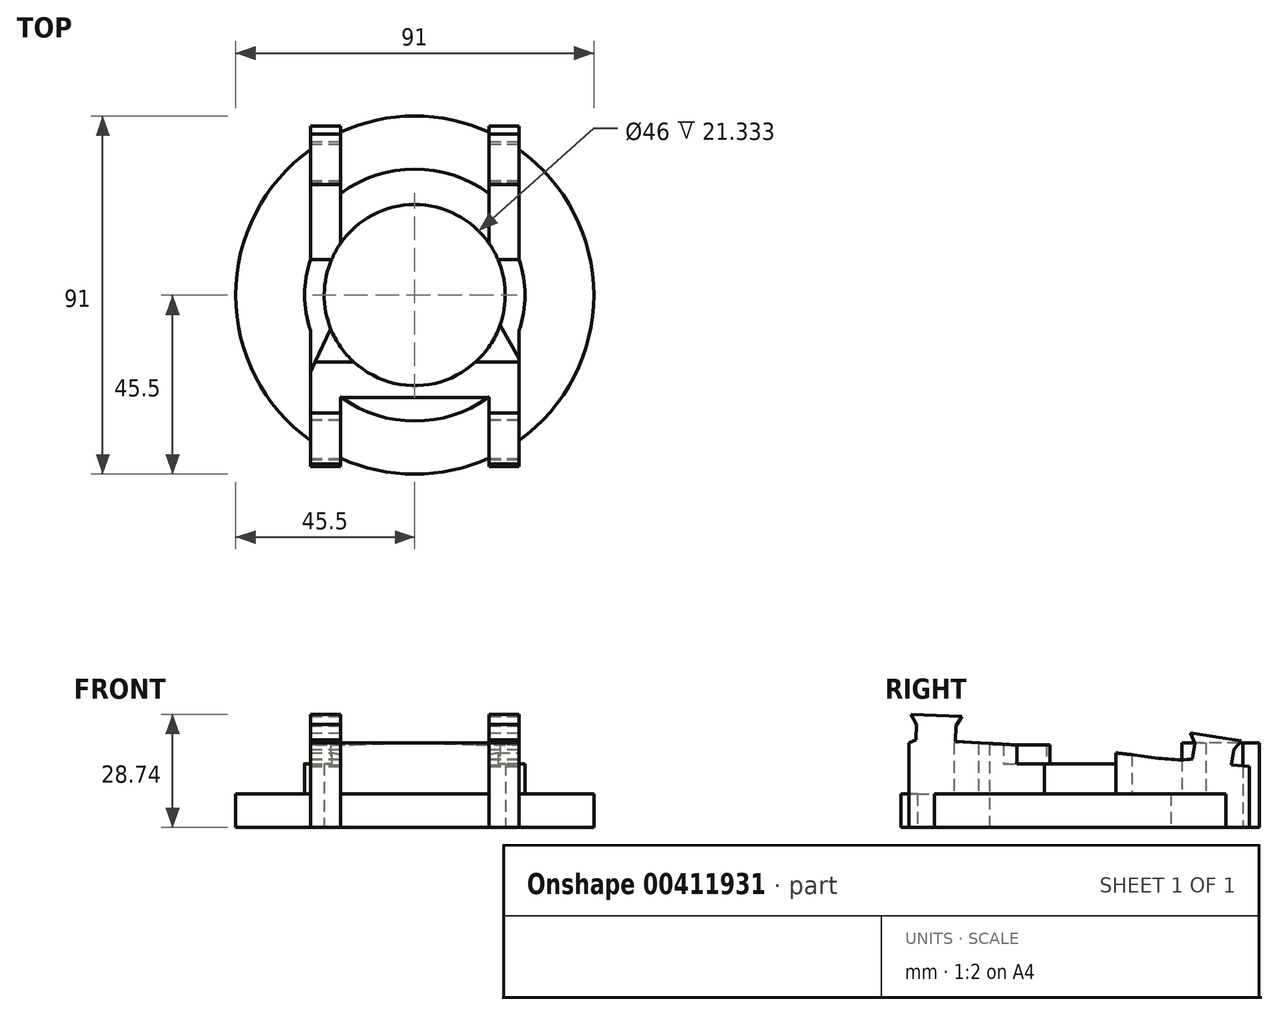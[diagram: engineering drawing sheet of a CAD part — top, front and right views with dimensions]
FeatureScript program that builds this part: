
annotation { "Feature Type Name" : "Feature", "Feature Type Description" : "" }
export const myFeature = defineFeature(function(context is Context, id is Id, definition is map)
    precondition{}
    {
        {
            var Q0;
            Q0=qCreatedBy(makeId("Top.planeOp"),FACE);
            var sketch = newSketch(context, id + "F0", { "sketchPlane" : qUnion([Q0])});
            skLineSegment(sketch, "E0", {"start": v(0, 45.5) * mm, "end": v(0, -45.5) * mm, "construction": true});
            skLineSegment(sketch, "E1", {"start": v(-45.7, 0) * mm, "end": v(45.55, 0) * mm, "construction": true});
            skCircle(sketch, "E2", {"center": v(0, 0) * mm, "radius": 23 * mm});
            skCircle(sketch, "E3", {"center": v(0, 0) * mm, "radius": 45.5 * mm});
            skArc(sketch, "E4", {"start": v(-26.5, 9.04) * mm, "mid": v(-28, 0) * mm, "end": v(-26.5, -9.04) * mm});
            skArc(sketch, "E5", {"start": v(-18.9, 25.82) * mm, "mid": v(0, 32) * mm, "end": v(18.9, 25.82) * mm});
            skArc(sketch, "E6", {"start": v(-18.9, -25.82) * mm, "mid": v(0, -32) * mm, "end": v(18.9, -25.82) * mm});
            skLineSegment(sketch, "E7.bottom", {"start": v(-26.5, 42.99) * mm, "end": v(-18.9, 42.99) * mm});
            skLineSegment(sketch, "E7.top", {"start": v(-26.5, -43.51) * mm, "end": v(-18.9, -43.51) * mm});
            skLineSegment(sketch, "E7.left", {"start": v(-26.5, 42.99) * mm, "end": v(-26.5, 9.04) * mm});
            skLineSegment(sketch, "E7.right", {"start": v(26.5, 42.99) * mm, "end": v(26.5, 9.04) * mm});
            skLineSegment(sketch, "E8.left", {"start": v(-18.9, 42.99) * mm, "end": v(-18.9, 13.1) * mm});
            skLineSegment(sketch, "E8.right", {"start": v(18.9, 42.99) * mm, "end": v(18.9, 13.1) * mm});
            skLineSegment(sketch, "E9", {"start": v(-26.5, 9.04) * mm, "end": v(-21.15, 9.04) * mm});
            skLineSegment(sketch, "E10", {"start": v(26.5, 9.04) * mm, "end": v(21.15, 9.04) * mm});
            skLineSegment(sketch, "E11.trimOffspring", {"start": v(-18.9, -13.1) * mm, "end": v(-18.9, -43.51) * mm});
            skLineSegment(sketch, "E12.trimOffspring", {"start": v(18.9, -13.1) * mm, "end": v(18.9, -43.51) * mm});
            skLineSegment(sketch, "E13.trimOffspring", {"start": v(-26.5, -9.04) * mm, "end": v(-26.5, -43.51) * mm});
            skLineSegment(sketch, "E14.trimOffspring", {"start": v(26.5, -9.04) * mm, "end": v(26.5, -43.51) * mm});
            skArc(sketch, "E15.trimOffspring", {"start": v(26.5, -9.04) * mm, "mid": v(28, 0) * mm, "end": v(26.5, 9.04) * mm});
            skLineSegment(sketch, "E16", {"start": v(-26.5, -19.54) * mm, "end": v(-21.34, -8.59) * mm});
            skLineSegment(sketch, "E17", {"start": v(26.5, -16.1) * mm, "end": v(21.69, -7.65) * mm});
            skLineSegment(sketch, "E18.trimOffspring", {"start": v(18.9, 42.99) * mm, "end": v(26.5, 42.99) * mm});
            skLineSegment(sketch, "E19.trimOffspring", {"start": v(18.9, -43.51) * mm, "end": v(26.5, -43.51) * mm});
            skSolve(sketch);
        }
        {
            var Q0;
            Q0=qCreatedBy(makeId("Right.planeOp"),FACE);
            var sketch = newSketch(context, id + "F1", { "sketchPlane" : qUnion([Q0])});
            skLineSegment(sketch, "E20", {"start": v(0, 0) * mm, "end": v(0, 30.19) * mm, "construction": true});
            skLineSegment(sketch, "E21", {"start": v(0, 30.19) * mm, "end": v(-43.27, 30.19) * mm, "construction": true});
            skSolve(sketch);
        }
        {
            var Q0;
            {var subQ1=sQuery(id+"F0.wireOp",EDGE,"E4");Q0=makeQuery(id+"F0.imprint","IMPRINT",FACE,{"disambiguationData":[TD([[makeQuery(id+"F0.imprint","IMPRINT",EDGE,{"derivedFrom":subQ1}),-1.0]])]});}
            var Q1;
            {var subQ5=sQuery(id+"F0.wireOp",EDGE,"E6");Q1=makeQuery(id+"F0.imprint","IMPRINT",FACE,{"disambiguationData":[TD([[makeQuery(id+"F0.imprint","IMPRINT",EDGE,{"derivedFrom":subQ5}),-1.0]])]});}
            var Q2;
            {var subQ4=sQuery(id+"F0.wireOp",EDGE,"E15.trimOffspring");Q2=makeQuery(id+"F0.imprint","IMPRINT",FACE,{"disambiguationData":[TD([[makeQuery(id+"F0.imprint","IMPRINT",EDGE,{"derivedFrom":subQ4}),-1.0]])]});}
            var Q3;
            {var subQ5=sQuery(id+"F0.wireOp",EDGE,"E5");Q3=makeQuery(id+"F0.imprint","IMPRINT",FACE,{"disambiguationData":[TD([[makeQuery(id+"F0.imprint","IMPRINT",EDGE,{"derivedFrom":subQ5}),1.0]])]});}
            var Q4;
            {var subQ6=sQuery(id+"F0.wireOp",EDGE,"E16");Q4=makeQuery(id+"F0.imprint","IMPRINT",FACE,{"disambiguationData":[TD([[makeQuery(id+"F0.imprint","IMPRINT",EDGE,{"derivedFrom":subQ6}),-1.0]])]});}
            var Q5;
            {var subQ5=sQuery(id+"F0.wireOp",EDGE,"E6");Q5=makeQuery(id+"F0.imprint","IMPRINT",FACE,{"disambiguationData":[TD([[makeQuery(id+"F0.imprint","IMPRINT",EDGE,{"derivedFrom":subQ5}),1.0]])]});}
            var Q6;
            {var subQ4=sQuery(id+"F0.wireOp",EDGE,"E17");Q6=makeQuery(id+"F0.imprint","IMPRINT",FACE,{"disambiguationData":[TD([[makeQuery(id+"F0.imprint","IMPRINT",EDGE,{"derivedFrom":subQ4}),1.0]])]});}
            var Q7;
            {var subQ0=sQuery(id+"F0.wireOp",EDGE,"E10");Q7=makeQuery(id+"F0.imprint","IMPRINT",FACE,{"disambiguationData":[TD([[makeQuery(id+"F0.imprint","IMPRINT",EDGE,{"derivedFrom":subQ0}),1.0]])]});}
            var Q8;
            {var subQ4=sQuery(id+"F0.wireOp",EDGE,"E10");Q8=makeQuery(id+"F0.imprint","IMPRINT",FACE,{"disambiguationData":[TD([[makeQuery(id+"F0.imprint","IMPRINT",EDGE,{"derivedFrom":subQ4}),-1.0]])]});}
            var Q9;
            {var subQ5=sQuery(id+"F0.wireOp",EDGE,"E5");Q9=makeQuery(id+"F0.imprint","IMPRINT",FACE,{"disambiguationData":[TD([[makeQuery(id+"F0.imprint","IMPRINT",EDGE,{"derivedFrom":subQ5}),-1.0]])]});}
            var Q10;
            {var subQ2=sQuery(id+"F0.wireOp",EDGE,"E9");Q10=makeQuery(id+"F0.imprint","IMPRINT",FACE,{"disambiguationData":[TD([[makeQuery(id+"F0.imprint","IMPRINT",EDGE,{"derivedFrom":subQ2}),1.0]])]});}
            var Q11;
            {var subQ2=sQuery(id+"F0.wireOp",EDGE,"E4");Q11=makeQuery(id+"F0.imprint","IMPRINT",FACE,{"disambiguationData":[TD([[makeQuery(id+"F0.imprint","IMPRINT",EDGE,{"derivedFrom":subQ2}),1.0]])]});}
            var Q12;
            {var subQ5=sQuery(id+"F0.wireOp",EDGE,"E7.bottom");Q12=makeQuery(id+"F0.imprint","IMPRINT",FACE,{"disambiguationData":[TD([[makeQuery(id+"F0.imprint","IMPRINT",EDGE,{"derivedFrom":subQ5}),-1.0]])]});}
            var Q13;
            {var subQ5=sQuery(id+"F0.wireOp",EDGE,"E18.trimOffspring");Q13=makeQuery(id+"F0.imprint","IMPRINT",FACE,{"disambiguationData":[TD([[makeQuery(id+"F0.imprint","IMPRINT",EDGE,{"derivedFrom":subQ5}),-1.0]])]});}
            var Q14;
            {var subQ5=sQuery(id+"F0.wireOp",EDGE,"E19.trimOffspring");Q14=makeQuery(id+"F0.imprint","IMPRINT",FACE,{"disambiguationData":[TD([[makeQuery(id+"F0.imprint","IMPRINT",EDGE,{"derivedFrom":subQ5}),1.0]])]});}
            var Q15;
            {var subQ5=sQuery(id+"F0.wireOp",EDGE,"E7.top");Q15=makeQuery(id+"F0.imprint","IMPRINT",FACE,{"disambiguationData":[TD([[makeQuery(id+"F0.imprint","IMPRINT",EDGE,{"derivedFrom":subQ5}),1.0]])]});}
            extrude(context, id + "F2", {"entities" : qUnion([Q0, Q1, Q2, Q3, Q4, Q5, Q6, Q7, Q8, Q9, Q10, Q11, Q12, Q13, Q14, Q15]), "depth" : 8.5 * mm});
        }
        {
            var Q0;
            {var subQ6=sQuery(id+"F0.wireOp",EDGE,"E16");Q0=makeQuery(id+"F0.imprint","IMPRINT",FACE,{"disambiguationData":[TD([[makeQuery(id+"F0.imprint","IMPRINT",EDGE,{"derivedFrom":subQ6}),-1.0]])]});}
            var Q1;
            {var subQ2=sQuery(id+"F0.wireOp",EDGE,"E9");Q1=makeQuery(id+"F0.imprint","IMPRINT",FACE,{"disambiguationData":[TD([[makeQuery(id+"F0.imprint","IMPRINT",EDGE,{"derivedFrom":subQ2}),1.0]])]});}
            var Q2;
            {var subQ4=sQuery(id+"F0.wireOp",EDGE,"E10");Q2=makeQuery(id+"F0.imprint","IMPRINT",FACE,{"disambiguationData":[TD([[makeQuery(id+"F0.imprint","IMPRINT",EDGE,{"derivedFrom":subQ4}),-1.0]])]});}
            var Q3;
            {var subQ4=sQuery(id+"F0.wireOp",EDGE,"E17");Q3=makeQuery(id+"F0.imprint","IMPRINT",FACE,{"disambiguationData":[TD([[makeQuery(id+"F0.imprint","IMPRINT",EDGE,{"derivedFrom":subQ4}),1.0]])]});}
            var Q4;
            {var subQ5=sQuery(id+"F0.wireOp",EDGE,"E7.top");Q4=makeQuery(id+"F0.imprint","IMPRINT",FACE,{"disambiguationData":[TD([[makeQuery(id+"F0.imprint","IMPRINT",EDGE,{"derivedFrom":subQ5}),1.0]])]});}
            var Q5;
            {var subQ5=sQuery(id+"F0.wireOp",EDGE,"E19.trimOffspring");Q5=makeQuery(id+"F0.imprint","IMPRINT",FACE,{"disambiguationData":[TD([[makeQuery(id+"F0.imprint","IMPRINT",EDGE,{"derivedFrom":subQ5}),1.0]])]});}
            var Q6;
            {var subQ5=sQuery(id+"F0.wireOp",EDGE,"E18.trimOffspring");Q6=makeQuery(id+"F0.imprint","IMPRINT",FACE,{"disambiguationData":[TD([[makeQuery(id+"F0.imprint","IMPRINT",EDGE,{"derivedFrom":subQ5}),-1.0]])]});}
            var Q7;
            {var subQ5=sQuery(id+"F0.wireOp",EDGE,"E7.bottom");Q7=makeQuery(id+"F0.imprint","IMPRINT",FACE,{"disambiguationData":[TD([[makeQuery(id+"F0.imprint","IMPRINT",EDGE,{"derivedFrom":subQ5}),-1.0]])]});}
            extrude(context, id + "F3", {"entities" : qUnion([Q0, Q1, Q2, Q3, Q4, Q5, Q6, Q7]), "operationType" : NewBodyOperationType.ADD, "depth" : 29 * mm});
        }
        {
            var Q0;
            {var subQ2=sQuery(id+"F0.wireOp",EDGE,"E4");Q0=makeQuery(id+"F0.imprint","IMPRINT",FACE,{"disambiguationData":[TD([[makeQuery(id+"F0.imprint","IMPRINT",EDGE,{"derivedFrom":subQ2}),1.0]])]});}
            var Q1;
            {var subQ0=sQuery(id+"F0.wireOp",EDGE,"E10");Q1=makeQuery(id+"F0.imprint","IMPRINT",FACE,{"disambiguationData":[TD([[makeQuery(id+"F0.imprint","IMPRINT",EDGE,{"derivedFrom":subQ0}),1.0]])]});}
            extrude(context, id + "F4", {"entities" : qUnion([Q0, Q1]), "operationType" : NewBodyOperationType.ADD, "depth" : 16.2 * mm});
        }
        {
            var Q0;
            {var subQ5=sQuery(id+"F0.wireOp",EDGE,"E5");Q0=makeQuery(id+"F0.imprint","IMPRINT",FACE,{"disambiguationData":[TD([[makeQuery(id+"F0.imprint","IMPRINT",EDGE,{"derivedFrom":subQ5}),-1.0]])]});}
            var Q1;
            {var subQ5=sQuery(id+"F0.wireOp",EDGE,"E6");Q1=makeQuery(id+"F0.imprint","IMPRINT",FACE,{"disambiguationData":[TD([[makeQuery(id+"F0.imprint","IMPRINT",EDGE,{"derivedFrom":subQ5}),1.0]])]});}
            extrude(context, id + "F5", {"entities" : qUnion([Q0, Q1]), "operationType" : NewBodyOperationType.ADD, "depth" : 21.5 * mm});
        }
        {
            var Q0;
            {var subQ0=sQuery(id+"F0.wireOp",EDGE,"E14.trimOffspring");Q0=makeQuery(id+"F4.boolean.opBoolean","MERGE",FACE,{"derivedFrom":[makeQuery(id+"F3.boolean.opBoolean","MERGE",FACE,{"derivedFrom":[makeQuery(id+"F2.opExtrude","SWEPT_FACE",FACE,{"disambiguationData":[OSD([subQ0])]}),makeQuery(id+"F3.opExtrude","SWEPT_FACE",FACE,{"disambiguationData":[OSD([subQ0])]})]}),makeQuery(id+"F4.opExtrude","SWEPT_FACE",FACE,{"disambiguationData":[OSD([subQ0])]})]});}
            var sketch = newSketch(context, id + "F6", { "sketchPlane" : qUnion([Q0])});
            skLineSegment(sketch, "E22", {"start": v(-17, 21) * mm, "end": v(-31.7, 21.81) * mm});
            skLineSegment(sketch, "E23", {"start": v(-31.7, 21.81) * mm, "end": v(-31.55, 25.81) * mm});
            skLineSegment(sketch, "E24", {"start": v(-31.55, 25.81) * mm, "end": v(-29.96, 28.26) * mm});
            skLineSegment(sketch, "E25", {"start": v(-29.96, 28.26) * mm, "end": v(-42.95, 28.74) * mm});
            skLineSegment(sketch, "E26", {"start": v(-41.55, 26.18) * mm, "end": v(-42.95, 28.74) * mm});
            skLineSegment(sketch, "E27", {"start": v(-41.55, 26.18) * mm, "end": v(-41.7, 22.19) * mm});
            skLineSegment(sketch, "E28", {"start": v(-41.7, 22.19) * mm, "end": v(-43.51, 21.5) * mm});
            skLineSegment(sketch, "E29", {"start": v(-36.46, 28.5) * mm, "end": v(-36.7, 22) * mm, "construction": true});
            skLineSegment(sketch, "E30", {"start": v(-43.51, 21.5) * mm, "end": v(-43.51, 29) * mm});
            skLineSegment(sketch, "E31", {"start": v(-43.51, 29) * mm, "end": v(-7.6, 29) * mm});
            skLineSegment(sketch, "E32", {"start": v(-7.6, 29) * mm, "end": v(-7.6, 21) * mm});
            skLineSegment(sketch, "E33", {"start": v(-7.6, 21) * mm, "end": v(-17, 21) * mm});
            skLineSegment(sketch, "E34", {"start": v(43, 15.5) * mm, "end": v(38.44, 15.84) * mm});
            skLineSegment(sketch, "E35", {"start": v(38.44, 15.84) * mm, "end": v(39.05, 19.8) * mm});
            skLineSegment(sketch, "E36", {"start": v(39.05, 19.8) * mm, "end": v(40.91, 22.03) * mm});
            skLineSegment(sketch, "E37", {"start": v(40.91, 22.03) * mm, "end": v(28.07, 24.01) * mm});
            skLineSegment(sketch, "E38", {"start": v(28.07, 24.01) * mm, "end": v(29.17, 21.32) * mm});
            skLineSegment(sketch, "E39", {"start": v(29.17, 21.32) * mm, "end": v(28.56, 17.36) * mm});
            skFitSpline(sketch, "E40", {"points": [v(28.56, 17.36) * mm, v(8.2, 19) * mm], "startDerivative": vector(-16.98, -2.06) * mm, "endDerivative": vector(-22.2, 1.8) * mm});
            skLineSegment(sketch, "E41", {"start": v(8.2, 19) * mm, "end": v(8.2, 29) * mm});
            skLineSegment(sketch, "E42", {"start": v(8.2, 29) * mm, "end": v(43, 29) * mm});
            skLineSegment(sketch, "E43", {"start": v(43, 29) * mm, "end": v(43, 15.5) * mm});
            skLineSegment(sketch, "E44", {"start": v(34.5, 23.02) * mm, "end": v(33.5, 16.6) * mm, "construction": true});
            skLineSegment(sketch, "E45", {"start": v(28.56, 17.36) * mm, "end": v(38.44, 15.84) * mm, "construction": true});
            skLineSegment(sketch, "E46", {"start": v(-41.7, 22.19) * mm, "end": v(-31.7, 21.81) * mm, "construction": true});
            skSolve(sketch);
        }
        {
            var Q0;
            {var subQ1=sQuery(id+"F6.wireOp",EDGE,"E22");Q0=makeQuery(id+"F6.imprint","IMPRINT",FACE,{"disambiguationData":[TD([[makeQuery(id+"F6.imprint","IMPRINT",EDGE,{"derivedFrom":subQ1}),-1.0]])]});}
            var Q1;
            {var subQ3=sQuery(id+"F6.wireOp",EDGE,"E32");Q1=makeQuery(id+"F6.imprint","IMPRINT",FACE,{"disambiguationData":[TD([[makeQuery(id+"F6.imprint","IMPRINT",EDGE,{"derivedFrom":subQ3}),-1.0]])]});}
            extrude(context, id + "F7", {"entities" : qUnion([Q0, Q1]), "operationType" : NewBodyOperationType.REMOVE, "oppositeDirection" : true, "depth" : 53 * mm});
        }
        {
            var Q0;
            Q0=makeQuery(id+"F6.imprint","IMPRINT",FACE,{"disambiguationData":[TD([[makeQuery(id+"F6.imprint","IMPRINT",EDGE,{"derivedFrom":sQuery(id+"F6.wireOp",EDGE,"E34")}),-1.0]])]});
            var Q1;
            {var subQ0=sQuery(id+"F0.wireOp",EDGE,"E8.right");Q1=makeQuery(id+"F3.boolean.opBoolean","MERGE",FACE,{"derivedFrom":[makeQuery(id+"F2.opExtrude","SWEPT_FACE",FACE,{"disambiguationData":[OSD([subQ0])]}),makeQuery(id+"F3.opExtrude","SWEPT_FACE",FACE,{"disambiguationData":[OSD([subQ0])]})]});}
            extrude(context, id + "F8", {"entities" : qUnion([Q0]), "operationType" : NewBodyOperationType.REMOVE, "endBound" : BoundingType.UP_TO_SURFACE, "oppositeDirection" : true, "endBoundEntityFace" : qUnion([Q1]), "depth" : 53.3 * mm});
        }
        {
            var Q0;
            Q0=makeQuery(id+"F6.imprint","IMPRINT",FACE,{"disambiguationData":[TD([[makeQuery(id+"F6.imprint","IMPRINT",EDGE,{"derivedFrom":sQuery(id+"F6.wireOp",EDGE,"E34")}),-1.0]])]});
            extrude(context, id + "F9", {"entities" : qUnion([Q0]), "operationType" : NewBodyOperationType.REMOVE, "oppositeDirection" : true, "depth" : 54.6 * mm, "hasSecondDirection" : true, "secondDirectionOppositeDirection" : true, "secondDirectionDepth" : 45.4 * mm});
        }
    });
